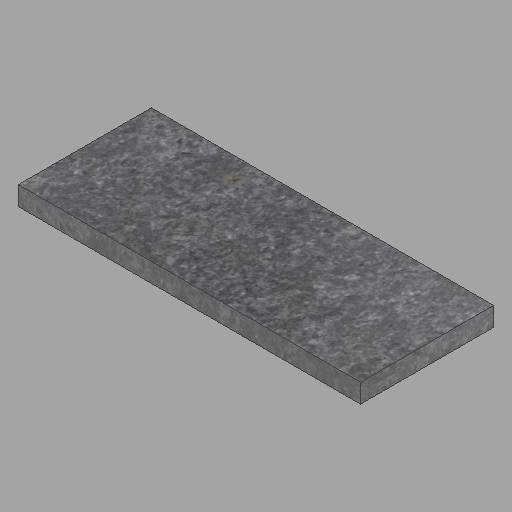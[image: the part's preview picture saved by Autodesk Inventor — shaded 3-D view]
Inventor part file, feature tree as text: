
AUTODESK INVENTOR PART (.ipt)
format: ipt  version: 2023 (Build 270158000, 158)  size: 222,208 bytes
history: native  units: in
note: dims shown in document units (in); Inventor stores cm internally (conversion verified against a paired STEP export)
features: extrude x1, sketch x1
ambient origin geometry x8: Origin, YZ Plane, XZ Plane, XY Plane, X Axis, Y Axis, Z Axis, Center Point
bodies: Solid1 (feature_tree)
feature tree (2):
  extrude  "Extrusion1"  Depth=14.0in
  sketch  "Sketch1"  dims[d0=2.0in d1=14.0in d2=36.0in d3=0.0in]
